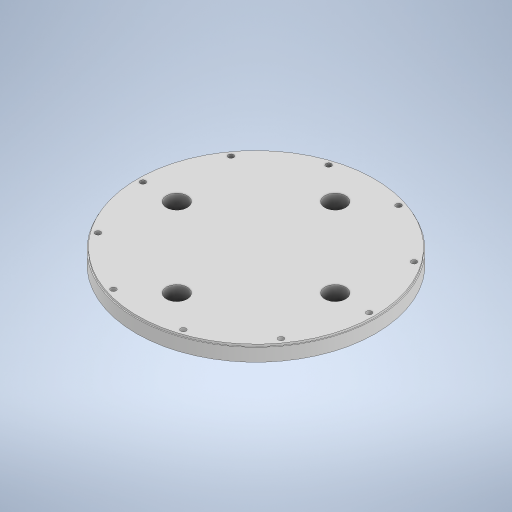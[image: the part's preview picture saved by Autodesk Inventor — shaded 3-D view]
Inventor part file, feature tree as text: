
AUTODESK INVENTOR PART (.ipt)
format: ipt  version: 2024.2 (Build 282272000, 272)  size: 294,400 bytes
history: native  units: in
note: dims shown in document units (in); Inventor stores cm internally (conversion verified against a paired STEP export)
features: extrude x3, sketch x3
ambient origin geometry x8: Origin, YZ Plane, XZ Plane, XY Plane, X Axis, Y Axis, Z Axis, Center Point
bodies: Solid1 (feature_tree)
feature tree (6):
  extrude  "Extrusion1"  Depth=0.5906in TaperAngle=0.0deg
  extrude  "Extrusion2"  Depth=0.0787in TaperAngle=0.0deg
  extrude  "Extrusion3"  Depth=3.937in TaperAngle=360.0deg
  sketch  "Sketch1"  dims[d1=3.937in d3=3.937in d19=360.0deg d21=360.0deg d22=0.5906in d23=0.0in]
  sketch  "Sketch2"  dims[d25=3.937in d27=3.937in d43=360.0deg d45=360.0deg d46=0.0787in d47=0.0in]
  sketch  "Sketch3"  dims[d49=3.937in d51=3.937in d52=360.0deg d53=360.0deg d55=3.937in d57=3.937in d58=360.0deg d59=360.0deg d60=1.1811in d61=0.0in d24=0.5in d48=0.5in d62=0.5in d63=0.0344in]
